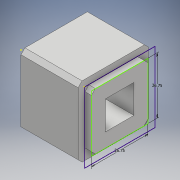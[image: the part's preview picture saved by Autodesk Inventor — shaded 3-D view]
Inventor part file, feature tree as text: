
AUTODESK INVENTOR PART (.ipt)
format: ipt  version: 2017 (Build 210142000, 142)  size: 138,240 bytes
history: native  units: mm
features: sketch x6, extrude x3, chamfer x1
ambient origin geometry x8: Origin, YZ Plane, XZ Plane, XY Plane, X Axis, Y Axis, Z Axis, Center Point
bodies: Solid1 (feature_tree)
feature tree (10):
  extrude  "Extrusion1"  Depth=33.25mm
  sketch  "Sketch2"  dims[d2=30.0mm d3=0.0mm d4=26.75mm]
  sketch  "Sketch3"  dims[d5=26.75mm]
  extrude  "Extrusion2"  Depth=26.75mm
  chamfer  "Chamfer1"  Distance=3.0mm
  extrude  "Extrusion3"  Depth=13.5mm
  sketch  "Sketch6"  dims[d10=1.875mm d11=2.0mm d12=45.0deg d13=13.5mm d14=13.5mm d15=6.625mm d16=6.625mm d17=26.75mm d18=0.0mm]
  sketch  "Sketch1"  dims[d0=33.25mm d1=33.25mm]
  sketch  "Sketch4"  dims[d6=26.75mm]
  sketch  "Sketch5"  dims[d7=26.75mm d8=3.0mm d9=0.0mm]
